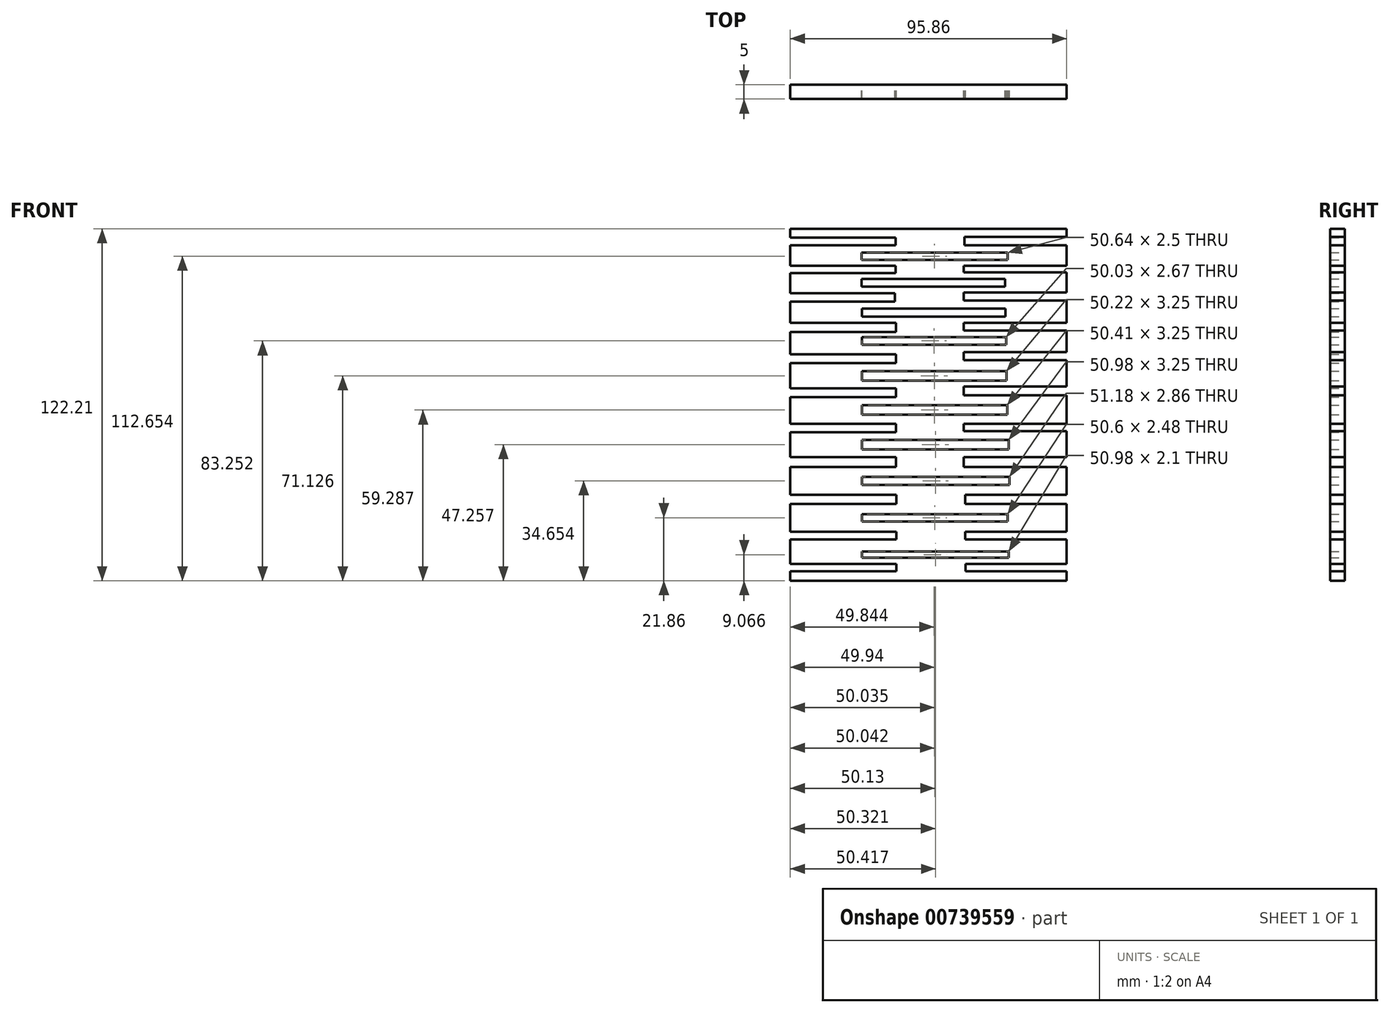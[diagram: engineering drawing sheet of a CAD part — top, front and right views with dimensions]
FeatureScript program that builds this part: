
annotation { "Feature Type Name" : "Feature", "Feature Type Description" : "" }
export const myFeature = defineFeature(function(context is Context, id is Id, definition is map)
    precondition{}
    {
        {
            var Q0;
            Q0=qCreatedBy(makeId("Front.planeOp"),FACE);
            var sketch = newSketch(context, id + "F0", { "sketchPlane" : qUnion([Q0])});
            skLineSegment(sketch, "E0.bottom", {"start": v(-48.03, -55.85) * mm, "end": v(47.83, -55.85) * mm});
            skLineSegment(sketch, "E0.top", {"start": v(-48.03, 66.36) * mm, "end": v(47.83, 66.36) * mm});
            skLineSegment(sketch, "E0.left", {"start": v(-48.03, -55.85) * mm, "end": v(-48.03, -52.54) * mm});
            skLineSegment(sketch, "E0.right", {"start": v(47.83, -55.85) * mm, "end": v(47.83, -52.54) * mm});
            skLineSegment(sketch, "E1.bottom", {"start": v(-23.2, -47.83) * mm, "end": v(27.78, -47.83) * mm});
            skLineSegment(sketch, "E1.top", {"start": v(-23.2, -45.73) * mm, "end": v(27.78, -45.73) * mm});
            skLineSegment(sketch, "E1.left", {"start": v(-23.2, -47.83) * mm, "end": v(-23.2, -45.73) * mm});
            skLineSegment(sketch, "E1.right", {"start": v(27.78, -47.83) * mm, "end": v(27.78, -45.73) * mm});
            skLineSegment(sketch, "E2.bottom", {"start": v(-48.03, -41.53) * mm, "end": v(-11.17, -41.53) * mm});
            skLineSegment(sketch, "E2.top", {"start": v(-48.03, -38.86) * mm, "end": v(-11.17, -38.86) * mm});
            skLineSegment(sketch, "E2.right", {"start": v(-11.17, -41.53) * mm, "end": v(-11.17, -38.86) * mm});
            skLineSegment(sketch, "E3.bottom", {"start": v(47.83, -38.86) * mm, "end": v(12.7, -38.86) * mm});
            skLineSegment(sketch, "E3.top", {"start": v(47.83, -41.53) * mm, "end": v(12.7, -41.53) * mm});
            skLineSegment(sketch, "E3.right", {"start": v(12.7, -38.86) * mm, "end": v(12.7, -41.53) * mm});
            skLineSegment(sketch, "E4.trimOffspring", {"start": v(47.83, -38.86) * mm, "end": v(47.83, -29.12) * mm});
            skLineSegment(sketch, "E5.trimOffspring", {"start": v(-48.03, -38.86) * mm, "end": v(-48.03, -29.12) * mm});
            skLineSegment(sketch, "E6.bottom", {"start": v(-23.2, -35.23) * mm, "end": v(27.4, -35.23) * mm});
            skLineSegment(sketch, "E6.top", {"start": v(-23.2, -32.75) * mm, "end": v(27.4, -32.75) * mm});
            skLineSegment(sketch, "E6.left", {"start": v(-23.2, -35.23) * mm, "end": v(-23.2, -32.75) * mm});
            skLineSegment(sketch, "E6.right", {"start": v(27.4, -35.23) * mm, "end": v(27.4, -32.75) * mm});
            skLineSegment(sketch, "E7.bottom", {"start": v(-11.17, -29.12) * mm, "end": v(-48.03, -29.12) * mm});
            skLineSegment(sketch, "E7.top", {"start": v(-11.17, -26.07) * mm, "end": v(-48.03, -26.07) * mm});
            skLineSegment(sketch, "E7.left", {"start": v(-11.17, -29.12) * mm, "end": v(-11.17, -26.07) * mm});
            skLineSegment(sketch, "E8.bottom", {"start": v(12.7, -29.12) * mm, "end": v(47.83, -29.12) * mm});
            skLineSegment(sketch, "E8.top", {"start": v(12.7, -26.07) * mm, "end": v(47.83, -26.07) * mm});
            skLineSegment(sketch, "E8.left", {"start": v(12.7, -29.12) * mm, "end": v(12.7, -26.07) * mm});
            skLineSegment(sketch, "E9.trimOffspring", {"start": v(47.83, -26.07) * mm, "end": v(47.83, -16.33) * mm});
            skLineSegment(sketch, "E10.trimOffspring", {"start": v(-48.03, -26.07) * mm, "end": v(-48.03, -16.33) * mm});
            skLineSegment(sketch, "E11.bottom", {"start": v(-23.2, -22.63) * mm, "end": v(27.97, -22.63) * mm});
            skLineSegment(sketch, "E11.top", {"start": v(-23.2, -19.76) * mm, "end": v(27.97, -19.76) * mm});
            skLineSegment(sketch, "E11.left", {"start": v(-23.2, -22.63) * mm, "end": v(-23.2, -19.76) * mm});
            skLineSegment(sketch, "E11.right", {"start": v(27.97, -22.63) * mm, "end": v(27.97, -19.76) * mm});
            skLineSegment(sketch, "E12.bottom", {"start": v(-11.36, -16.33) * mm, "end": v(-48.03, -16.33) * mm});
            skLineSegment(sketch, "E12.top", {"start": v(-11.36, -12.89) * mm, "end": v(-48.03, -12.89) * mm});
            skLineSegment(sketch, "E12.left", {"start": v(-11.36, -16.33) * mm, "end": v(-11.36, -12.89) * mm});
            skLineSegment(sketch, "E13.trimOffspring", {"start": v(-48.03, -12.89) * mm, "end": v(-48.03, -4.3) * mm});
            skLineSegment(sketch, "E14.bottom", {"start": v(12.13, -16.33) * mm, "end": v(47.83, -16.33) * mm});
            skLineSegment(sketch, "E14.top", {"start": v(12.13, -12.89) * mm, "end": v(47.83, -12.89) * mm});
            skLineSegment(sketch, "E14.left", {"start": v(12.13, -16.33) * mm, "end": v(12.13, -12.89) * mm});
            skLineSegment(sketch, "E15.trimOffspring", {"start": v(47.83, -12.89) * mm, "end": v(47.83, -3.91) * mm});
            skLineSegment(sketch, "E16.bottom", {"start": v(-23.2, -10.22) * mm, "end": v(27.78, -10.22) * mm});
            skLineSegment(sketch, "E16.top", {"start": v(-23.2, -6.97) * mm, "end": v(27.78, -6.97) * mm});
            skLineSegment(sketch, "E16.left", {"start": v(-23.2, -10.22) * mm, "end": v(-23.2, -6.97) * mm});
            skLineSegment(sketch, "E16.right", {"start": v(27.78, -10.22) * mm, "end": v(27.78, -6.97) * mm});
            skLineSegment(sketch, "E17.bottom", {"start": v(-11.36, -4.3) * mm, "end": v(-48.03, -4.3) * mm});
            skLineSegment(sketch, "E17.top", {"start": v(-11.36, -1.43) * mm, "end": v(-48.03, -1.43) * mm});
            skLineSegment(sketch, "E17.left", {"start": v(-11.36, -4.3) * mm, "end": v(-11.36, -1.43) * mm});
            skLineSegment(sketch, "E18.trimOffspring", {"start": v(-48.03, -1.43) * mm, "end": v(-48.03, 7.92) * mm});
            skLineSegment(sketch, "E19.bottom", {"start": v(12.13, -3.91) * mm, "end": v(47.83, -3.91) * mm});
            skLineSegment(sketch, "E19.top", {"start": v(12.13, -1.43) * mm, "end": v(47.83, -1.43) * mm});
            skLineSegment(sketch, "E19.left", {"start": v(12.13, -3.91) * mm, "end": v(12.13, -1.43) * mm});
            skLineSegment(sketch, "E20.trimOffspring", {"start": v(47.83, -1.43) * mm, "end": v(47.83, 8.5) * mm});
            skLineSegment(sketch, "E21.bottom", {"start": v(-23.2, 1.81) * mm, "end": v(27.21, 1.81) * mm});
            skLineSegment(sketch, "E21.top", {"start": v(-23.2, 5.06) * mm, "end": v(27.21, 5.06) * mm});
            skLineSegment(sketch, "E21.left", {"start": v(-23.2, 1.81) * mm, "end": v(-23.2, 5.06) * mm});
            skLineSegment(sketch, "E21.right", {"start": v(27.21, 1.81) * mm, "end": v(27.21, 5.06) * mm});
            skLineSegment(sketch, "E22.bottom", {"start": v(-11.36, 7.92) * mm, "end": v(-48.03, 7.92) * mm});
            skLineSegment(sketch, "E22.top", {"start": v(-11.36, 10.98) * mm, "end": v(-48.03, 10.98) * mm});
            skLineSegment(sketch, "E22.left", {"start": v(-11.36, 7.92) * mm, "end": v(-11.36, 10.98) * mm});
            skLineSegment(sketch, "E23.bottom", {"start": v(12.13, 8.5) * mm, "end": v(47.83, 8.5) * mm});
            skLineSegment(sketch, "E23.top", {"start": v(12.13, 11.55) * mm, "end": v(47.83, 11.55) * mm});
            skLineSegment(sketch, "E23.left", {"start": v(12.13, 8.5) * mm, "end": v(12.13, 11.55) * mm});
            skLineSegment(sketch, "E24.trimOffspring", {"start": v(-48.03, 10.98) * mm, "end": v(-48.03, 19.76) * mm});
            skLineSegment(sketch, "E25.trimOffspring", {"start": v(47.83, 11.55) * mm, "end": v(47.83, 20.72) * mm});
            skLineSegment(sketch, "E26.bottom", {"start": v(-23.2, 13.65) * mm, "end": v(27.02, 13.65) * mm});
            skLineSegment(sketch, "E26.top", {"start": v(-23.2, 16.9) * mm, "end": v(27.02, 16.9) * mm});
            skLineSegment(sketch, "E26.left", {"start": v(-23.2, 13.65) * mm, "end": v(-23.2, 16.9) * mm});
            skLineSegment(sketch, "E26.right", {"start": v(27.02, 13.65) * mm, "end": v(27.02, 16.9) * mm});
            skLineSegment(sketch, "E27.bottom", {"start": v(-11.36, 19.76) * mm, "end": v(-48.03, 19.76) * mm});
            skLineSegment(sketch, "E27.top", {"start": v(-11.36, 22.82) * mm, "end": v(-48.03, 22.82) * mm});
            skLineSegment(sketch, "E27.left", {"start": v(-11.36, 19.76) * mm, "end": v(-11.36, 22.82) * mm});
            skLineSegment(sketch, "E28.bottom", {"start": v(12.13, 20.72) * mm, "end": v(47.83, 20.72) * mm});
            skLineSegment(sketch, "E28.top", {"start": v(12.13, 23.58) * mm, "end": v(47.83, 23.58) * mm});
            skLineSegment(sketch, "E28.left", {"start": v(12.13, 20.72) * mm, "end": v(12.13, 23.58) * mm});
            skLineSegment(sketch, "E29.trimOffspring", {"start": v(47.83, 23.58) * mm, "end": v(47.83, 31.03) * mm});
            skLineSegment(sketch, "E30.trimOffspring", {"start": v(-48.03, 22.82) * mm, "end": v(-48.03, 30.46) * mm});
            skLineSegment(sketch, "E31.bottom", {"start": v(-23.2, 26.07) * mm, "end": v(26.83, 26.07) * mm});
            skLineSegment(sketch, "E31.top", {"start": v(-23.2, 28.74) * mm, "end": v(26.83, 28.74) * mm});
            skLineSegment(sketch, "E31.left", {"start": v(-23.2, 26.07) * mm, "end": v(-23.2, 28.74) * mm});
            skLineSegment(sketch, "E31.right", {"start": v(26.83, 26.07) * mm, "end": v(26.83, 28.74) * mm});
            skLineSegment(sketch, "E32.bottom", {"start": v(12.13, 31.03) * mm, "end": v(47.83, 31.03) * mm});
            skLineSegment(sketch, "E32.top", {"start": v(12.13, 33.7) * mm, "end": v(47.83, 33.7) * mm});
            skLineSegment(sketch, "E32.left", {"start": v(12.13, 31.03) * mm, "end": v(12.13, 33.7) * mm});
            skLineSegment(sketch, "E33.bottom", {"start": v(-11.36, 30.46) * mm, "end": v(-48.03, 30.46) * mm});
            skLineSegment(sketch, "E33.top", {"start": v(-11.36, 33.7) * mm, "end": v(-48.03, 33.7) * mm});
            skLineSegment(sketch, "E33.left", {"start": v(-11.36, 30.46) * mm, "end": v(-11.36, 33.7) * mm});
            skLineSegment(sketch, "E34.bottom", {"start": v(-23.2, 35.8) * mm, "end": v(26.64, 35.8) * mm});
            skLineSegment(sketch, "E34.top", {"start": v(-23.2, 38.67) * mm, "end": v(26.64, 38.67) * mm});
            skLineSegment(sketch, "E34.left", {"start": v(-23.2, 35.8) * mm, "end": v(-23.2, 38.67) * mm});
            skLineSegment(sketch, "E34.right", {"start": v(26.64, 35.8) * mm, "end": v(26.64, 38.67) * mm});
            skLineSegment(sketch, "E35.trimOffspring", {"start": v(-48.03, 33.7) * mm, "end": v(-48.03, 41.02) * mm});
            skLineSegment(sketch, "E36.trimOffspring", {"start": v(47.83, 33.7) * mm, "end": v(47.83, 41.48) * mm});
            skLineSegment(sketch, "E37.bottom", {"start": v(-11.73, 41.02) * mm, "end": v(-48.03, 41.02) * mm});
            skLineSegment(sketch, "E37.top", {"start": v(-11.73, 43.97) * mm, "end": v(-48.03, 43.97) * mm});
            skLineSegment(sketch, "E37.left", {"start": v(-11.73, 41.02) * mm, "end": v(-11.73, 43.97) * mm});
            skLineSegment(sketch, "E38.trimOffspring", {"start": v(-48.03, 43.97) * mm, "end": v(-48.03, 51.01) * mm});
            skLineSegment(sketch, "E39.bottom", {"start": v(12.12, 41.48) * mm, "end": v(47.83, 41.48) * mm});
            skLineSegment(sketch, "E39.top", {"start": v(12.12, 44.2) * mm, "end": v(47.83, 44.2) * mm});
            skLineSegment(sketch, "E39.left", {"start": v(12.12, 41.48) * mm, "end": v(12.12, 44.2) * mm});
            skLineSegment(sketch, "E40.trimOffspring", {"start": v(47.83, 44.2) * mm, "end": v(47.83, 51.24) * mm});
            skLineSegment(sketch, "E41.bottom", {"start": v(-23.3, 46.24) * mm, "end": v(26.42, 46.24) * mm});
            skLineSegment(sketch, "E41.top", {"start": v(-23.3, 48.97) * mm, "end": v(26.42, 48.97) * mm});
            skLineSegment(sketch, "E41.left", {"start": v(-23.3, 46.24) * mm, "end": v(-23.3, 48.97) * mm});
            skLineSegment(sketch, "E41.right", {"start": v(26.42, 46.24) * mm, "end": v(26.42, 48.97) * mm});
            skLineSegment(sketch, "E42.bottom", {"start": v(-11.5, 51.01) * mm, "end": v(-48.03, 51.01) * mm});
            skLineSegment(sketch, "E42.top", {"start": v(-11.5, 53.51) * mm, "end": v(-48.03, 53.51) * mm});
            skLineSegment(sketch, "E42.left", {"start": v(-11.5, 51.01) * mm, "end": v(-11.5, 53.51) * mm});
            skLineSegment(sketch, "E43.trimOffspring", {"start": v(-48.03, 53.51) * mm, "end": v(-48.03, 60.55) * mm});
            skLineSegment(sketch, "E44.bottom", {"start": v(12.13, 51.24) * mm, "end": v(47.83, 51.24) * mm});
            skLineSegment(sketch, "E44.top", {"start": v(12.13, 53.51) * mm, "end": v(47.83, 53.51) * mm});
            skLineSegment(sketch, "E44.left", {"start": v(12.13, 51.24) * mm, "end": v(12.13, 53.51) * mm});
            skLineSegment(sketch, "E45.trimOffspring", {"start": v(47.83, 53.51) * mm, "end": v(47.83, 60.55) * mm});
            skLineSegment(sketch, "E46.bottom", {"start": v(-23.3, 55.55) * mm, "end": v(27.33, 55.55) * mm});
            skLineSegment(sketch, "E46.top", {"start": v(-23.3, 58.05) * mm, "end": v(27.33, 58.05) * mm});
            skLineSegment(sketch, "E46.left", {"start": v(-23.3, 55.55) * mm, "end": v(-23.3, 58.05) * mm});
            skLineSegment(sketch, "E46.right", {"start": v(27.33, 55.55) * mm, "end": v(27.33, 58.05) * mm});
            skLineSegment(sketch, "E47.bottom", {"start": v(-11.5, 60.55) * mm, "end": v(-48.03, 60.55) * mm});
            skLineSegment(sketch, "E47.top", {"start": v(-11.5, 63.28) * mm, "end": v(-48.03, 63.28) * mm});
            skLineSegment(sketch, "E47.left", {"start": v(-11.5, 60.55) * mm, "end": v(-11.5, 63.28) * mm});
            skLineSegment(sketch, "E48.trimOffspring", {"start": v(-48.03, 63.28) * mm, "end": v(-48.03, 66.36) * mm});
            skLineSegment(sketch, "E49.bottom", {"start": v(12.34, 60.55) * mm, "end": v(47.83, 60.55) * mm});
            skLineSegment(sketch, "E49.top", {"start": v(12.34, 63.5) * mm, "end": v(47.83, 63.5) * mm});
            skLineSegment(sketch, "E49.left", {"start": v(12.34, 60.55) * mm, "end": v(12.34, 63.5) * mm});
            skLineSegment(sketch, "E50.trimOffspring", {"start": v(47.83, 63.5) * mm, "end": v(47.83, 66.36) * mm});
            skLineSegment(sketch, "E51.bottom", {"start": v(-11.27, -50.04) * mm, "end": v(-48.03, -50.04) * mm});
            skLineSegment(sketch, "E51.top", {"start": v(-11.27, -52.54) * mm, "end": v(-48.03, -52.54) * mm});
            skLineSegment(sketch, "E51.left", {"start": v(-11.27, -50.04) * mm, "end": v(-11.27, -52.54) * mm});
            skLineSegment(sketch, "E52.trimOffspring", {"start": v(-48.03, -50.04) * mm, "end": v(-48.03, -41.53) * mm});
            skLineSegment(sketch, "E53.bottom", {"start": v(12.8, -50.04) * mm, "end": v(47.83, -50.04) * mm});
            skLineSegment(sketch, "E53.top", {"start": v(12.8, -52.54) * mm, "end": v(47.83, -52.54) * mm});
            skLineSegment(sketch, "E53.left", {"start": v(12.8, -50.04) * mm, "end": v(12.8, -52.54) * mm});
            skLineSegment(sketch, "E54.trimOffspring", {"start": v(47.83, -50.04) * mm, "end": v(47.83, -41.53) * mm});
            skSolve(sketch);
        }
        {
            var Q0;
            Q0 = qSketchRegion(id + "F0", true);
            extrude(context, id + "F1", {"entities" : qUnion([Q0]), "depth" : 5 * mm, "offsetDistance" : 25.4 * mm});
        }
    });
